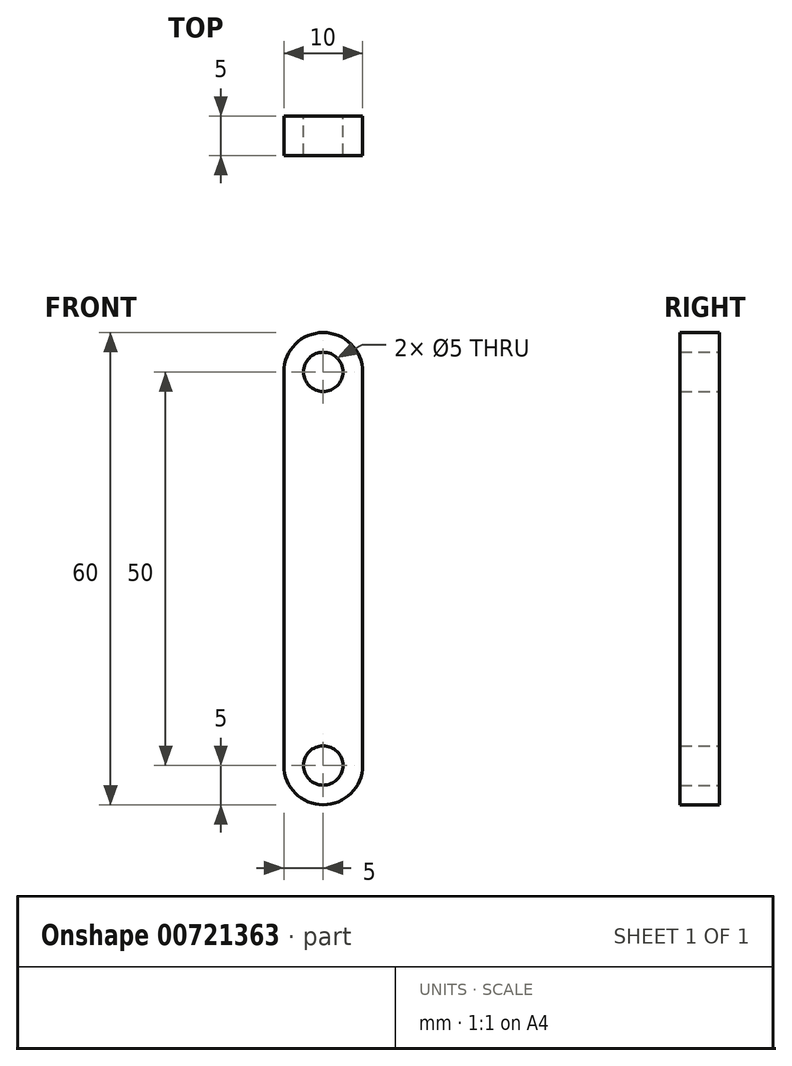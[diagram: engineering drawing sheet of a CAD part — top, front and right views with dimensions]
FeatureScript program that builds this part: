
annotation { "Feature Type Name" : "Feature", "Feature Type Description" : "" }
export const myFeature = defineFeature(function(context is Context, id is Id, definition is map)
    precondition{}
    {
        {
            var Q0;
            Q0=qCreatedBy(makeId("Front.planeOp"),FACE);
            var sketch = newSketch(context, id + "F0", { "sketchPlane" : qUnion([Q0])});
            skLineSegment(sketch, "E0.left", {"start": v(5, 25) * mm, "end": v(5, -25) * mm});
            skLineSegment(sketch, "E0.right", {"start": v(-5, 25) * mm, "end": v(-5, -25) * mm});
            skPoint(sketch, "E0.middle", {"position": v(0, 0) * mm});
            skArc(sketch, "E1", {"start": v(5, 25) * mm, "mid": v(0, 30) * mm, "end": v(-5, 25) * mm});
            skArc(sketch, "E2", {"start": v(-5, -25) * mm, "mid": v(0, -30) * mm, "end": v(5, -25) * mm});
            skCircle(sketch, "E3", {"center": v(0, 25) * mm, "radius": 2.5 * mm});
            skCircle(sketch, "E4", {"center": v(0, -25) * mm, "radius": 2.5 * mm});
            skSolve(sketch);
        }
        {
            var Q0;
            Q0 = qSketchRegion(id + "F0", true);
            extrude(context, id + "F1", {"entities" : qUnion([Q0]), "depth" : 5 * mm, "offsetDistance" : 25.4 * mm});
        }
    });
